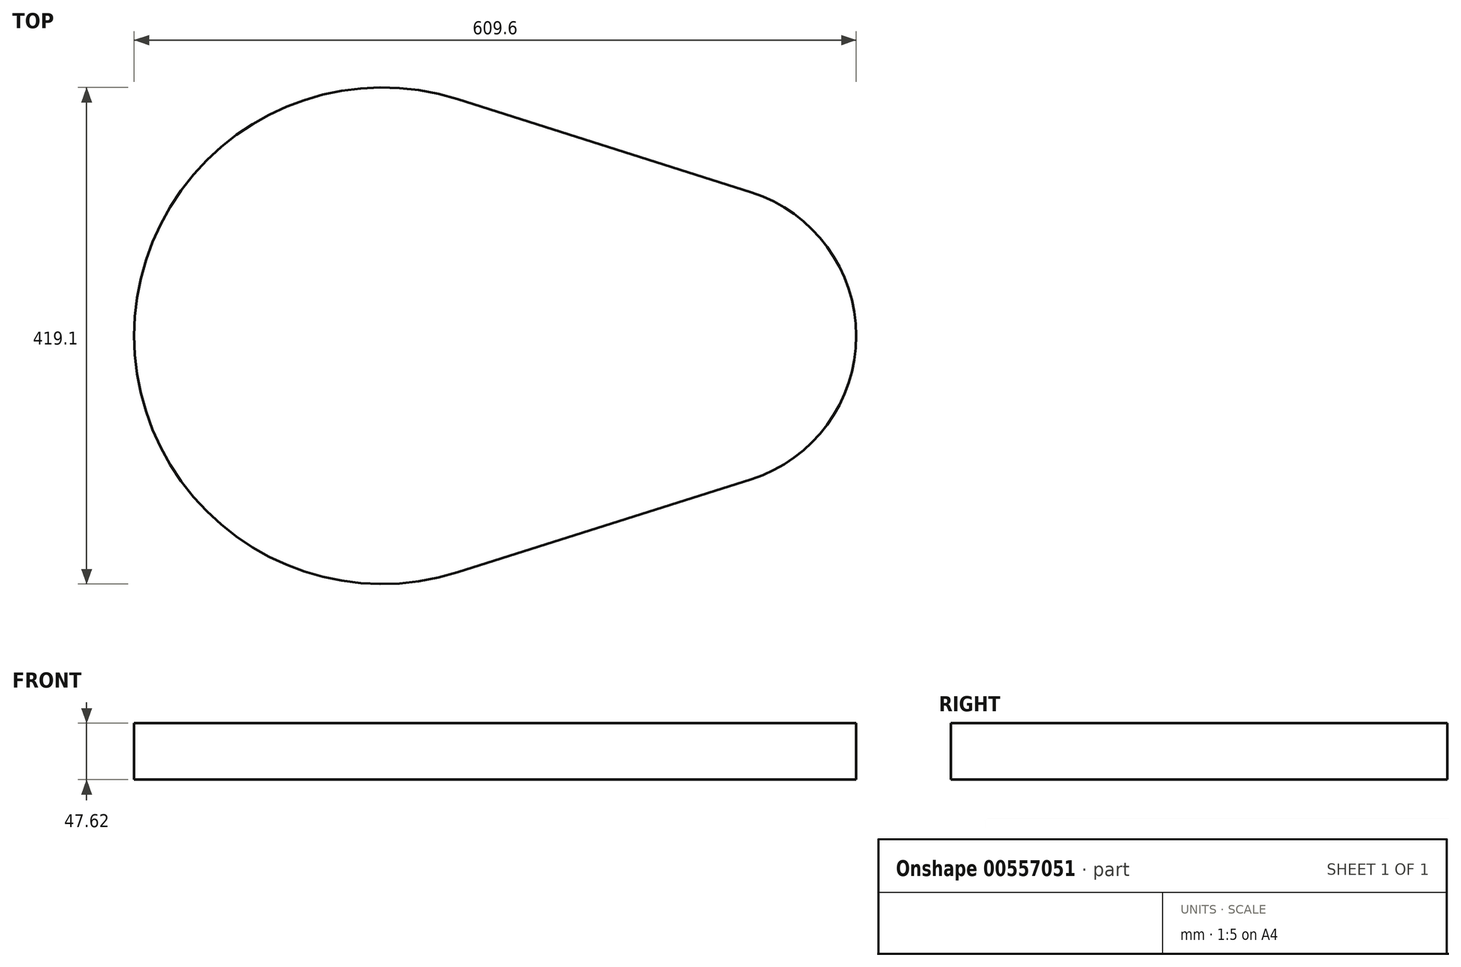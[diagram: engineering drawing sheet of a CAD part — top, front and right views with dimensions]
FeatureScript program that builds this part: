
annotation { "Feature Type Name" : "Feature", "Feature Type Description" : "" }
export const myFeature = defineFeature(function(context is Context, id is Id, definition is map)
    precondition{}
    {
        {
            var Q0;
            Q0=qCreatedBy(makeId("Top.planeOp"),FACE);
            var sketch = newSketch(context, id + "F0", { "sketchPlane" : qUnion([Q0])});
            skLineSegment(sketch, "E0", {"start": v(-304.8, 0) * mm, "end": v(304.8, 0) * mm, "construction": true});
            skPoint(sketch, "E1", {"position": v(177.8, 0) * mm});
            skPoint(sketch, "E2", {"position": v(-95.25, 0) * mm});
            skLineSegment(sketch, "E3", {"start": v(-95.25, 209.55) * mm, "end": v(-95.25, -209.55) * mm, "construction": true});
            skArc(sketch, "E4", {"start": v(-31.9, 199.74) * mm, "mid": v(-304.8, 0) * mm, "end": v(-31.9, -199.74) * mm});
            skArc(sketch, "E5", {"start": v(216.2, -121.06) * mm, "mid": v(304.8, 0) * mm, "end": v(216.2, 121.06) * mm});
            skLineSegment(sketch, "E6", {"start": v(-31.9, 199.74) * mm, "end": v(216.2, 121.06) * mm});
            skLineSegment(sketch, "E7", {"start": v(216.2, -121.06) * mm, "end": v(-31.9, -199.74) * mm});
            skSolve(sketch);
        }
        {
            var Q0;
            Q0 = qSketchRegion(id + "F0", true);
            extrude(context, id + "F1", {"entities" : qUnion([Q0]), "depth" : 47.62 * mm, "offsetDistance" : 25.4 * mm});
        }
    });
